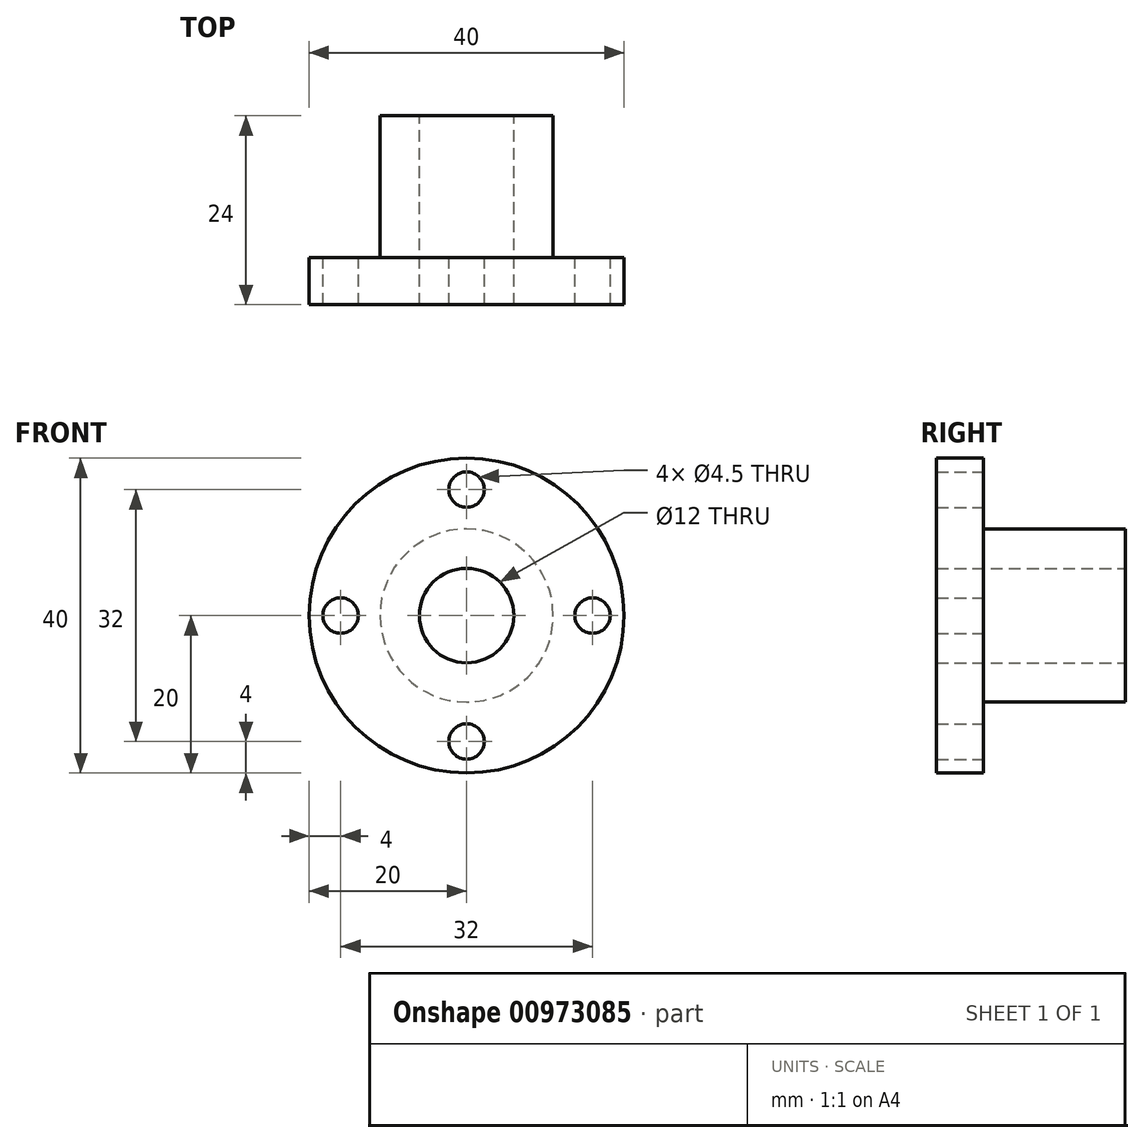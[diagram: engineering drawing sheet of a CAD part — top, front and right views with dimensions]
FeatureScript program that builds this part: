
annotation { "Feature Type Name" : "Feature", "Feature Type Description" : "" }
export const myFeature = defineFeature(function(context is Context, id is Id, definition is map)
    precondition{}
    {
        {
            var Q0;
            Q0=qCreatedBy(makeId("Front.planeOp"),FACE);
            var sketch = newSketch(context, id + "F0", { "sketchPlane" : qUnion([Q0])});
            skCircle(sketch, "E0", {"center": v(0, 0) * mm, "radius": 20 * mm});
            skCircle(sketch, "E1", {"center": v(0, 0) * mm, "radius": 11 * mm});
            skCircle(sketch, "E2", {"center": v(0, 0) * mm, "radius": 6 * mm});
            skLineSegment(sketch, "E3", {"start": v(0, 20) * mm, "end": v(0, -20) * mm, "construction": true});
            skLineSegment(sketch, "E4", {"start": v(-20, 0) * mm, "end": v(20, 0) * mm, "construction": true});
            skSolve(sketch);
        }
        {
            var Q0;
            Q0=makeQuery(id+"F0.imprint","IMPRINT",FACE,{"disambiguationData":[TD([[makeQuery(id+"F0.imprint","IMPRINT",EDGE,{"derivedFrom":sQuery(id+"F0.wireOp",EDGE,"E0")}),1.0]])]});
            var Q1;
            Q1=makeQuery(id+"F0.imprint","IMPRINT",FACE,{"disambiguationData":[TD([[makeQuery(id+"F0.imprint","IMPRINT",EDGE,{"derivedFrom":sQuery(id+"F0.wireOp",EDGE,"E1")}),1.0]])]});
            var Q2;
            Q2=makeQuery(id+"F0.imprint","IMPRINT",FACE,{"disambiguationData":[TD([[makeQuery(id+"F0.imprint","IMPRINT",EDGE,{"derivedFrom":sQuery(id+"F0.wireOp",EDGE,"E2")}),1.0]])]});
            extrude(context, id + "F1", {"entities" : qUnion([Q0, Q1, Q2]), "depth" : 24 * mm, "offsetDistance" : 25 * mm});
        }
        {
            var Q0;
            Q0=makeQuery(id+"F1.opExtrude","CAP_FACE",FACE,{"disambiguationData":[OSD([sQuery(id+"F0.wireOp",EDGE,"E0")])],"isStart":true});
            var sketch = newSketch(context, id + "F2", { "sketchPlane" : qUnion([Q0])});
            skCircle(sketch, "E5", {"center": v(0, 0) * mm, "radius": 11 * mm});
            skCircle(sketch, "E6", {"center": v(0, 0) * mm, "radius": 6 * mm});
            skSolve(sketch);
        }
        {
            var Q0;
            Q0=makeQuery(id+"F2.imprint","IMPRINT",FACE,{"disambiguationData":[TD([[makeQuery(id+"F2.imprint","IMPRINT",EDGE,{"derivedFrom":sQuery(id+"F2.wireOp",EDGE,"E6")}),1.0]])]});
            extrude(context, id + "F3", {"entities" : qUnion([Q0]), "operationType" : NewBodyOperationType.REMOVE, "endBound" : BoundingType.THROUGH_ALL, "oppositeDirection" : true, "depth" : 25 * mm, "offsetDistance" : 25 * mm});
        }
        {
            var Q0;
            Q0=makeQuery(id+"F1.opExtrude","CAP_FACE",FACE,{"disambiguationData":[OSD([sQuery(id+"F0.wireOp",EDGE,"E0")])],"isStart":true});
            var sketch = newSketch(context, id + "F4", { "sketchPlane" : qUnion([Q0])});
            skCircle(sketch, "E7", {"center": v(0, 0) * mm, "radius": 11 * mm});
            skSolve(sketch);
        }
        {
            var Q0;
            Q0=makeQuery(id+"F4.imprint","IMPRINT",FACE,{"disambiguationData":[TD([[makeQuery(id+"F4.imprint","IMPRINT",EDGE,{"derivedFrom":sQuery(id+"F4.wireOp",EDGE,"E7")}),-1.0]])]});
            extrude(context, id + "F5", {"entities" : qUnion([Q0]), "operationType" : NewBodyOperationType.REMOVE, "oppositeDirection" : true, "depth" : 18 * mm, "offsetDistance" : 25 * mm});
        }
        {
            var Q0;
            Q0=makeQuery(id+"F5.boolean.opBoolean","COPY",FACE,{"derivedFrom":makeQuery(id+"F5.opExtrude","CAP_FACE",FACE,{"disambiguationData":[OSD([sQuery(id+"F0.wireOp",EDGE,"E0"),sQuery(id+"F4.wireOp",EDGE,"E7")])],"isStart":false})});
            var sketch = newSketch(context, id + "F6", { "sketchPlane" : qUnion([Q0])});
            skLineSegment(sketch, "E8", {"start": v(0, 0) * mm, "end": v(0, 20) * mm, "construction": true});
            skLineSegment(sketch, "E9", {"start": v(0, 20) * mm, "end": v(0, -20) * mm, "construction": true});
            skLineSegment(sketch, "E10", {"start": v(-20, 0) * mm, "end": v(20, 0) * mm, "construction": true});
            skLineSegment(sketch, "E11", {"start": v(-16, -19.8) * mm, "end": v(-16, 21.25) * mm, "construction": true});
            skLineSegment(sketch, "E12", {"start": v(16, -20.7) * mm, "end": v(16, 22.6) * mm, "construction": true});
            skLineSegment(sketch, "E13", {"start": v(-25.1, -16) * mm, "end": v(21.03, -16) * mm, "construction": true});
            skLineSegment(sketch, "E14", {"start": v(-26.22, 16) * mm, "end": v(23.1, 16) * mm, "construction": true});
            skCircle(sketch, "E15", {"center": v(-16, 0) * mm, "radius": 2.25 * mm});
            skCircle(sketch, "E16", {"center": v(0, 16) * mm, "radius": 2.25 * mm});
            skCircle(sketch, "E17", {"center": v(16, 0) * mm, "radius": 2.25 * mm});
            skCircle(sketch, "E18", {"center": v(0, -16) * mm, "radius": 2.25 * mm});
            skSolve(sketch);
        }
        {
            var Q0;
            Q0=makeQuery(id+"F6.imprint","IMPRINT",FACE,{"disambiguationData":[TD([[makeQuery(id+"F6.imprint","IMPRINT",EDGE,{"derivedFrom":sQuery(id+"F6.wireOp",EDGE,"E15")}),1.0]])]});
            var Q1;
            Q1=makeQuery(id+"F6.imprint","IMPRINT",FACE,{"disambiguationData":[TD([[makeQuery(id+"F6.imprint","IMPRINT",EDGE,{"derivedFrom":sQuery(id+"F6.wireOp",EDGE,"E18")}),1.0]])]});
            var Q2;
            Q2=makeQuery(id+"F6.imprint","IMPRINT",FACE,{"disambiguationData":[TD([[makeQuery(id+"F6.imprint","IMPRINT",EDGE,{"derivedFrom":sQuery(id+"F6.wireOp",EDGE,"E17")}),1.0]])]});
            var Q3;
            Q3=makeQuery(id+"F6.imprint","IMPRINT",FACE,{"disambiguationData":[TD([[makeQuery(id+"F6.imprint","IMPRINT",EDGE,{"derivedFrom":sQuery(id+"F6.wireOp",EDGE,"E16")}),1.0]])]});
            extrude(context, id + "F7", {"entities" : qUnion([Q0, Q1, Q2, Q3]), "operationType" : NewBodyOperationType.REMOVE, "endBound" : BoundingType.THROUGH_ALL, "oppositeDirection" : true, "depth" : 25 * mm, "offsetDistance" : 25 * mm});
        }
    });
